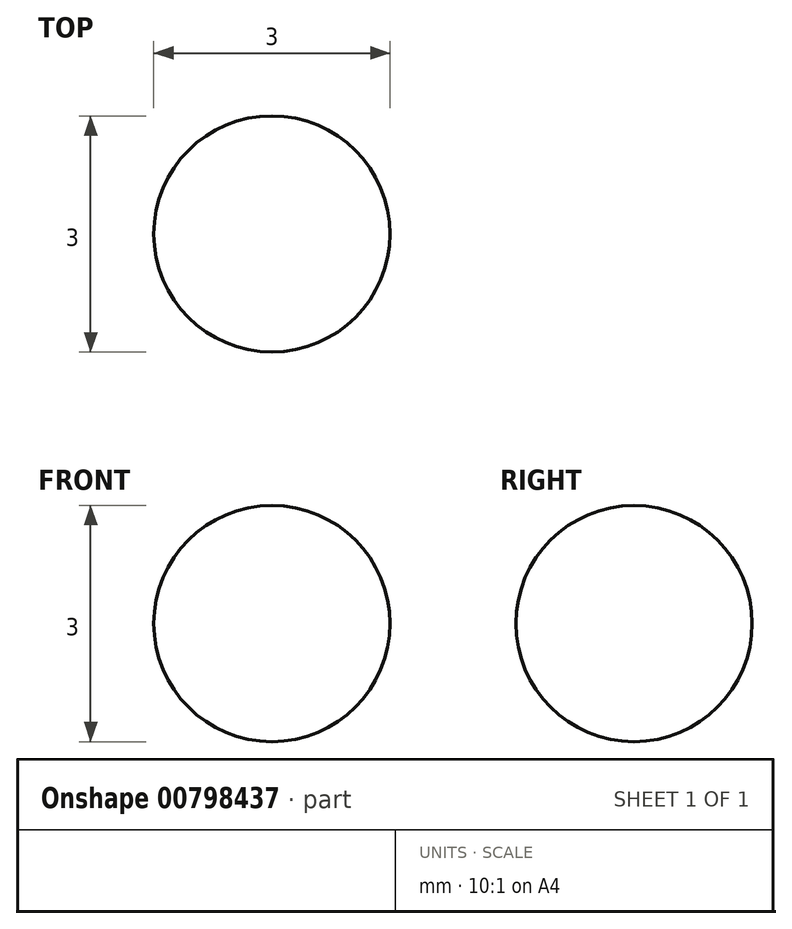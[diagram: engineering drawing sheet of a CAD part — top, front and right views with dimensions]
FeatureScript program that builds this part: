
annotation { "Feature Type Name" : "Feature", "Feature Type Description" : "" }
export const myFeature = defineFeature(function(context is Context, id is Id, definition is map)
    precondition{}
    {
        {
            var Q0;
            Q0=qCreatedBy(makeId("Top.planeOp"),FACE);
            var sketch = newSketch(context, id + "F0", { "sketchPlane" : qUnion([Q0])});
            skLineSegment(sketch, "E0", {"start": v(0, 0) * mm, "end": v(0, 3) * mm});
            skArc(sketch, "E1", {"start": v(0, 0) * mm, "mid": v(1.5, 1.5) * mm, "end": v(0, 3) * mm});
            skSolve(sketch);
        }
        {
            var Q0;
            Q0=makeQuery(id+"F0.imprint","IMPRINT",FACE,{"disambiguationData":[TD([[makeQuery(id+"F0.imprint","IMPRINT",EDGE,{"derivedFrom":sQuery(id+"F0.wireOp",EDGE,"E0")}),-1.0]])]});
            var Q1;
            Q1=sQuery(id+"F0.wireOp",EDGE,"E0");
            revolve(context, id + "F1", {"surfaceOperationType" : NewSurfaceOperationType.NEW, "entities" : qUnion([Q0]), "axis" : qUnion([Q1]), "revolveType" : RevolveType.FULL});
        }
    });
